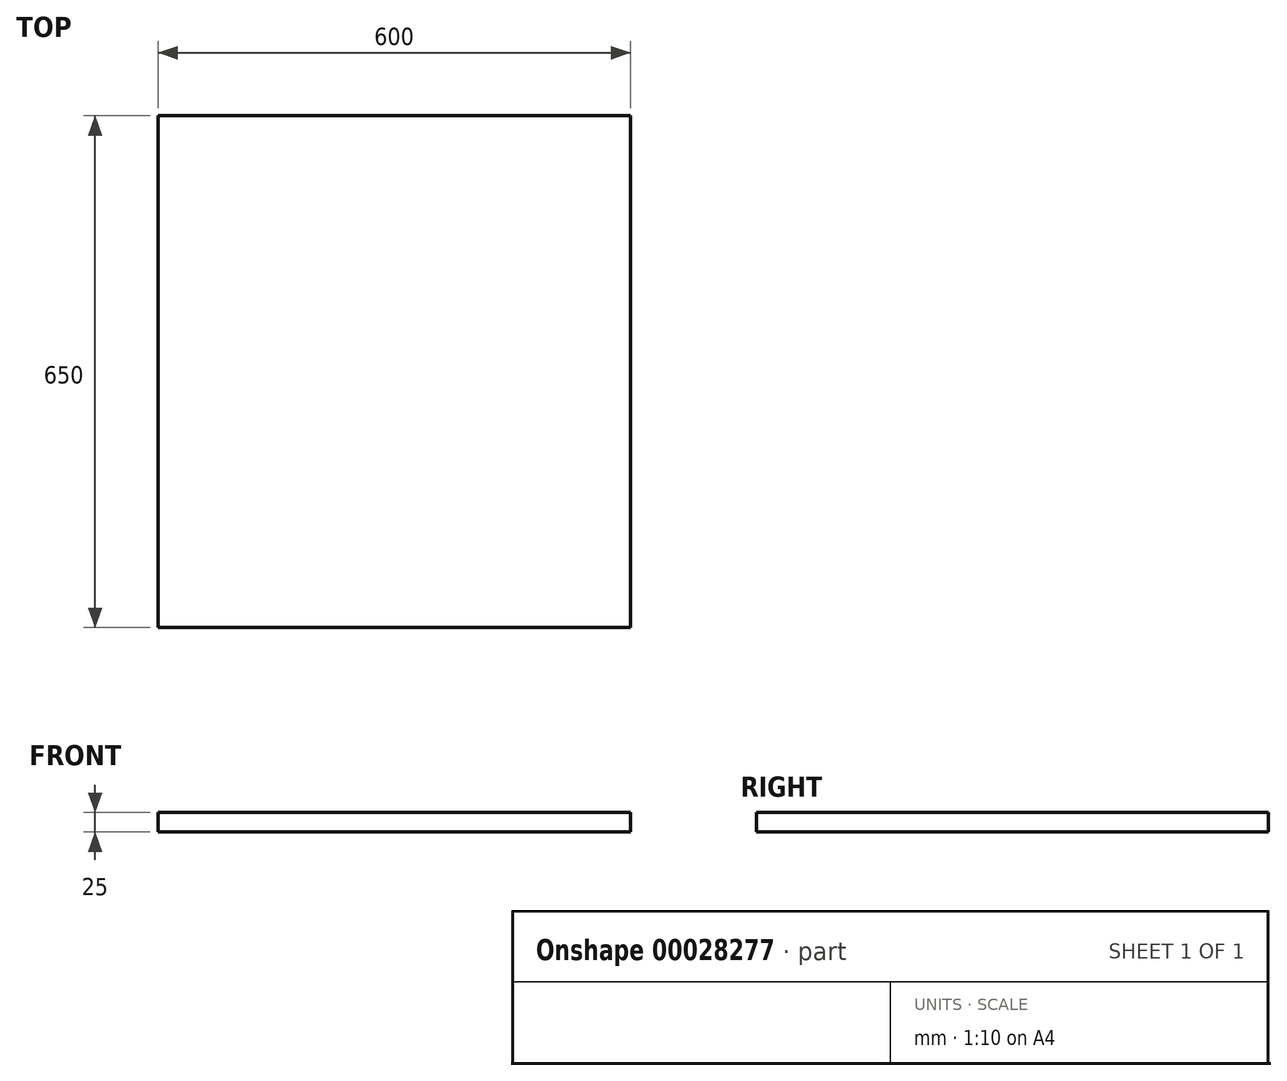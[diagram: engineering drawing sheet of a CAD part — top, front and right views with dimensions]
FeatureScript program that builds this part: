
annotation { "Feature Type Name" : "Feature", "Feature Type Description" : "" }
export const myFeature = defineFeature(function(context is Context, id is Id, definition is map)
    precondition{}
    {
        {
            var Q0;
            Q0=qCreatedBy(makeId("Top.planeOp"),FACE);
            var sketch = newSketch(context, id + "F0", { "sketchPlane" : qUnion([Q0])});
            skLineSegment(sketch, "E0.bottom", {"start": v(0, 0) * mm, "end": v(600, 0) * mm});
            skLineSegment(sketch, "E0.top", {"start": v(0, 650) * mm, "end": v(600, 650) * mm});
            skLineSegment(sketch, "E0.left", {"start": v(0, 0) * mm, "end": v(0, 650) * mm});
            skLineSegment(sketch, "E0.right", {"start": v(600, 0) * mm, "end": v(600, 650) * mm});
            skSolve(sketch);
        }
        {
            var Q0;
            Q0 = qSketchRegion(id + "F0", true);
            extrude(context, id + "F1", {"entities" : qUnion([Q0]), "depth" : 25 * mm});
        }
    });
